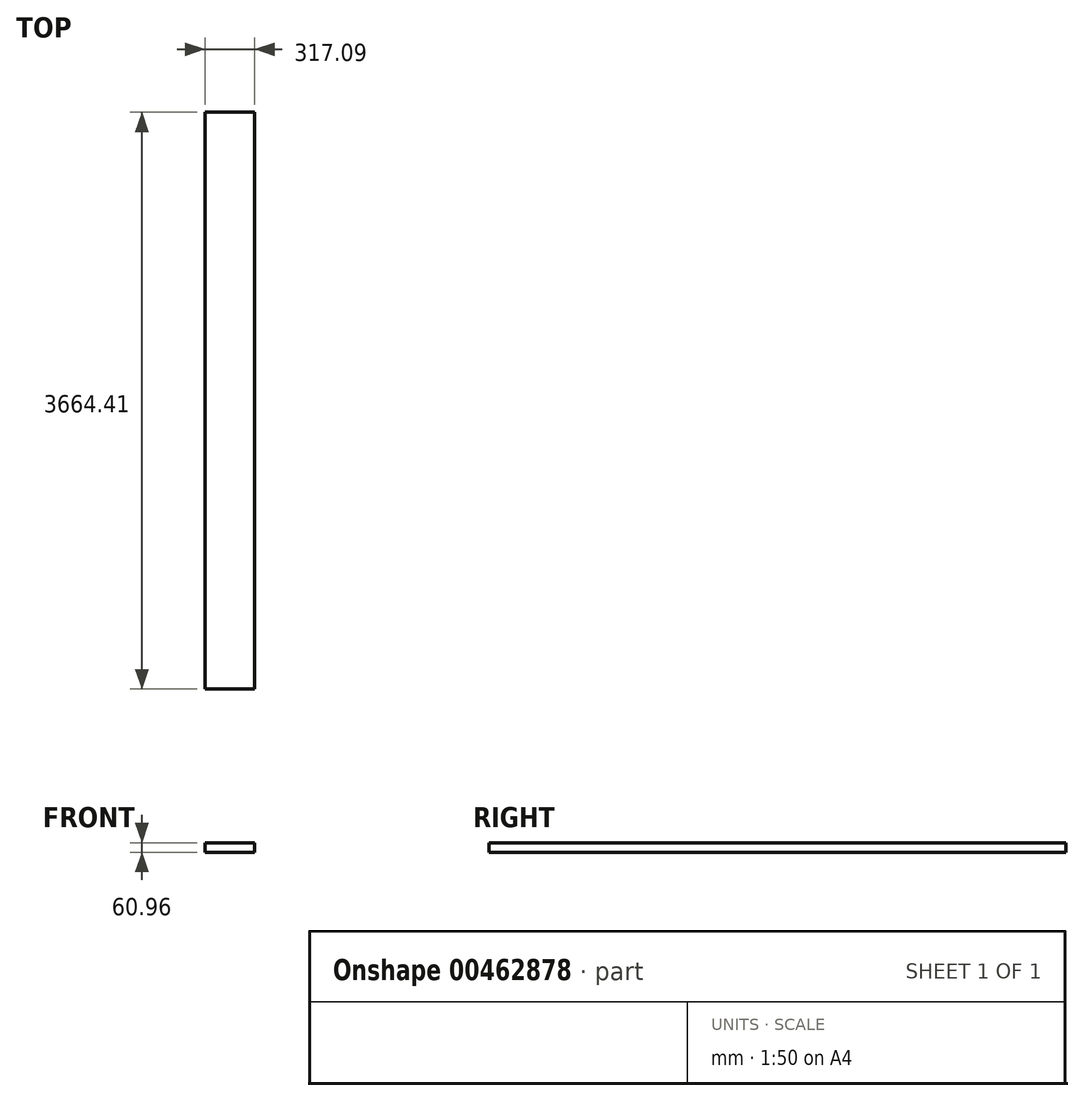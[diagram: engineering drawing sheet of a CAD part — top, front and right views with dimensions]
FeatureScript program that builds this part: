
annotation { "Feature Type Name" : "Feature", "Feature Type Description" : "" }
export const myFeature = defineFeature(function(context is Context, id is Id, definition is map)
    precondition{}
    {
        {
            var Q0;
            Q0=qCreatedBy(makeId("Top.planeOp"),FACE);
            var sketch = newSketch(context, id + "F0", { "sketchPlane" : qUnion([Q0])});
            skLineSegment(sketch, "E0.bottom", {"start": v(-184.48, 3188.2) * mm, "end": v(132.61, 3188.2) * mm});
            skLineSegment(sketch, "E0.top", {"start": v(-184.48, -476.2) * mm, "end": v(132.61, -476.2) * mm});
            skLineSegment(sketch, "E0.left", {"start": v(132.61, 3188.2) * mm, "end": v(132.61, -476.2) * mm});
            skLineSegment(sketch, "E0.right", {"start": v(-184.48, 3188.2) * mm, "end": v(-184.48, -476.2) * mm});
            skSolve(sketch);
        }
        {
            var Q0;
            Q0=makeQuery(id+"F0.imprint","IMPRINT",FACE,{"disambiguationData":[TD([[makeQuery(id+"F0.imprint","IMPRINT",EDGE,{"derivedFrom":sQuery(id+"F0.wireOp",EDGE,"E0.bottom")}),-1.0]])]});
            extrude(context, id + "F1", {"entities" : qUnion([Q0]), "depth" : 60.96 * mm});
        }
    });
